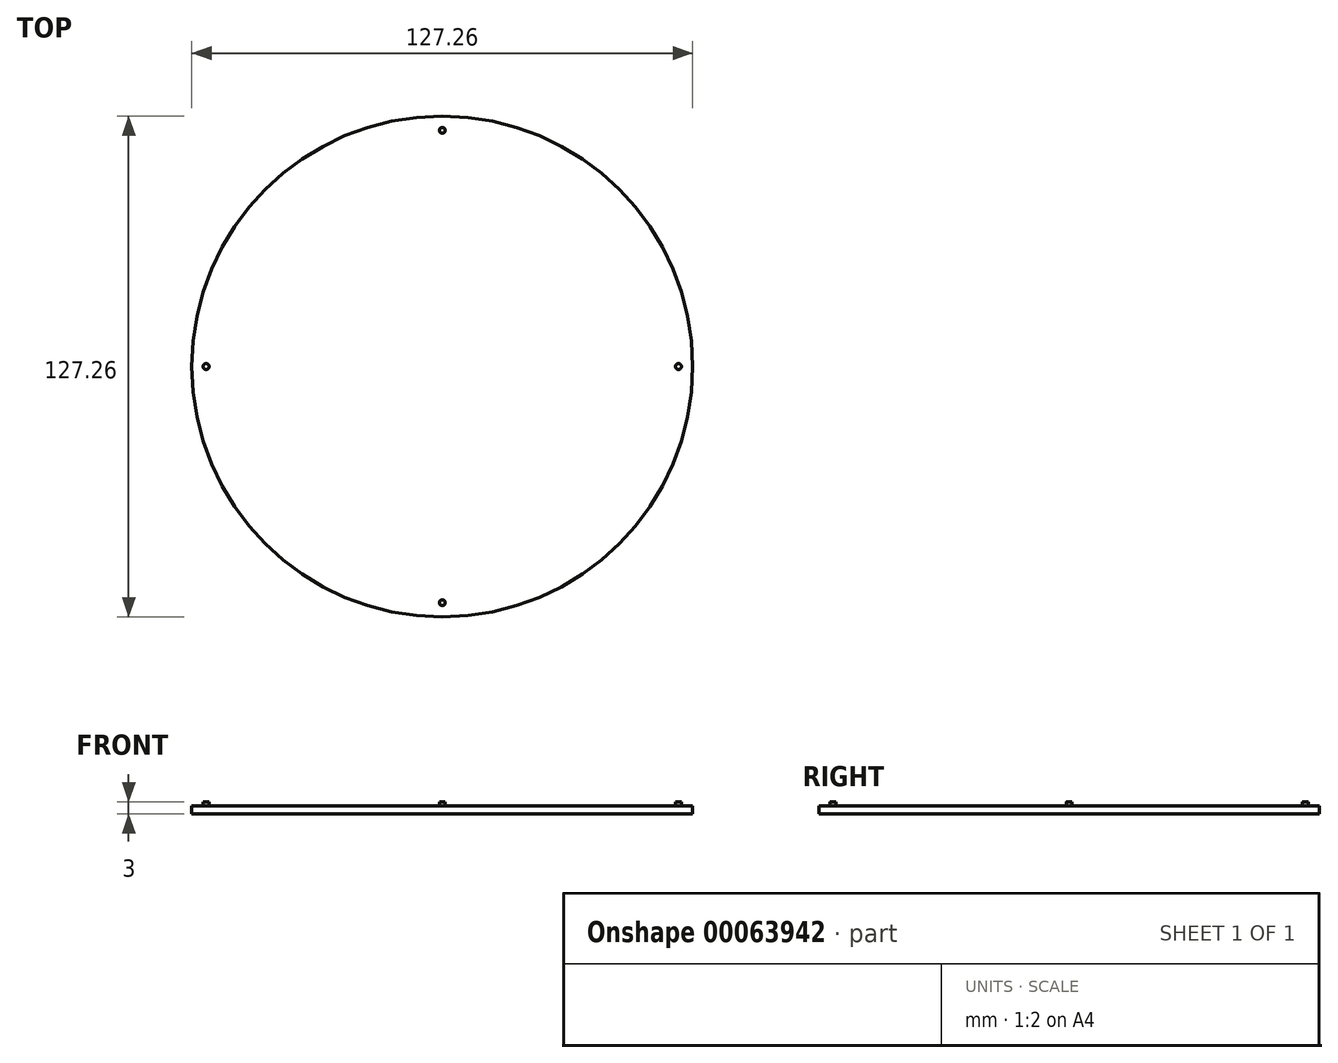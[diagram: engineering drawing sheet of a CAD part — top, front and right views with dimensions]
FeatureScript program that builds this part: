
annotation { "Feature Type Name" : "Feature", "Feature Type Description" : "" }
export const myFeature = defineFeature(function(context is Context, id is Id, definition is map)
    precondition{}
    {
        {
            var Q0;
            Q0=qCreatedBy(makeId("Top.planeOp"),FACE);
            var sketch = newSketch(context, id + "F0", { "sketchPlane" : qUnion([Q0])});
            skCircle(sketch, "E0", {"center": v(0, 0) * mm, "radius": 63.62 * mm});
            skSolve(sketch);
        }
        {
            var Q0;
            Q0=makeQuery(id+"F0.imprint","IMPRINT",FACE,{"disambiguationData":[TD([[makeQuery(id+"F0.imprint","IMPRINT",EDGE,{"derivedFrom":sQuery(id+"F0.wireOp",EDGE,"E0")}),1.0]])]});
            extrude(context, id + "F1", {"entities" : qUnion([Q0]), "depth" : 2 * mm});
        }
        {
            var Q0;
            Q0=makeQuery(id+"F1.opExtrude","CAP_FACE",FACE,{"disambiguationData":[OSD([sQuery(id+"F0.wireOp",EDGE,"E0")])],"isStart":false});
            var sketch = newSketch(context, id + "F2", { "sketchPlane" : qUnion([Q0])});
            skCircle(sketch, "E1", {"center": v(0, 60) * mm, "radius": 0.75 * mm});
            skCircle(sketch, "E2.1.0", {"center": v(-60, 0) * mm, "radius": 0.75 * mm});
            skCircle(sketch, "E2.2.0", {"center": v(0, -60) * mm, "radius": 0.75 * mm});
            skPoint(sketch, "E2.center", {"position": v(0, 0) * mm});
            skCircle(sketch, "E3.1.3.0", {"center": v(60, 0) * mm, "radius": 0.75 * mm});
            skSolve(sketch);
        }
        {
            var Q0;
            Q0 = qSketchRegion(id + "F2", true);
            extrude(context, id + "F3", {"entities" : qUnion([Q0]), "operationType" : NewBodyOperationType.ADD, "depth" : 1 * mm});
        }
    });
